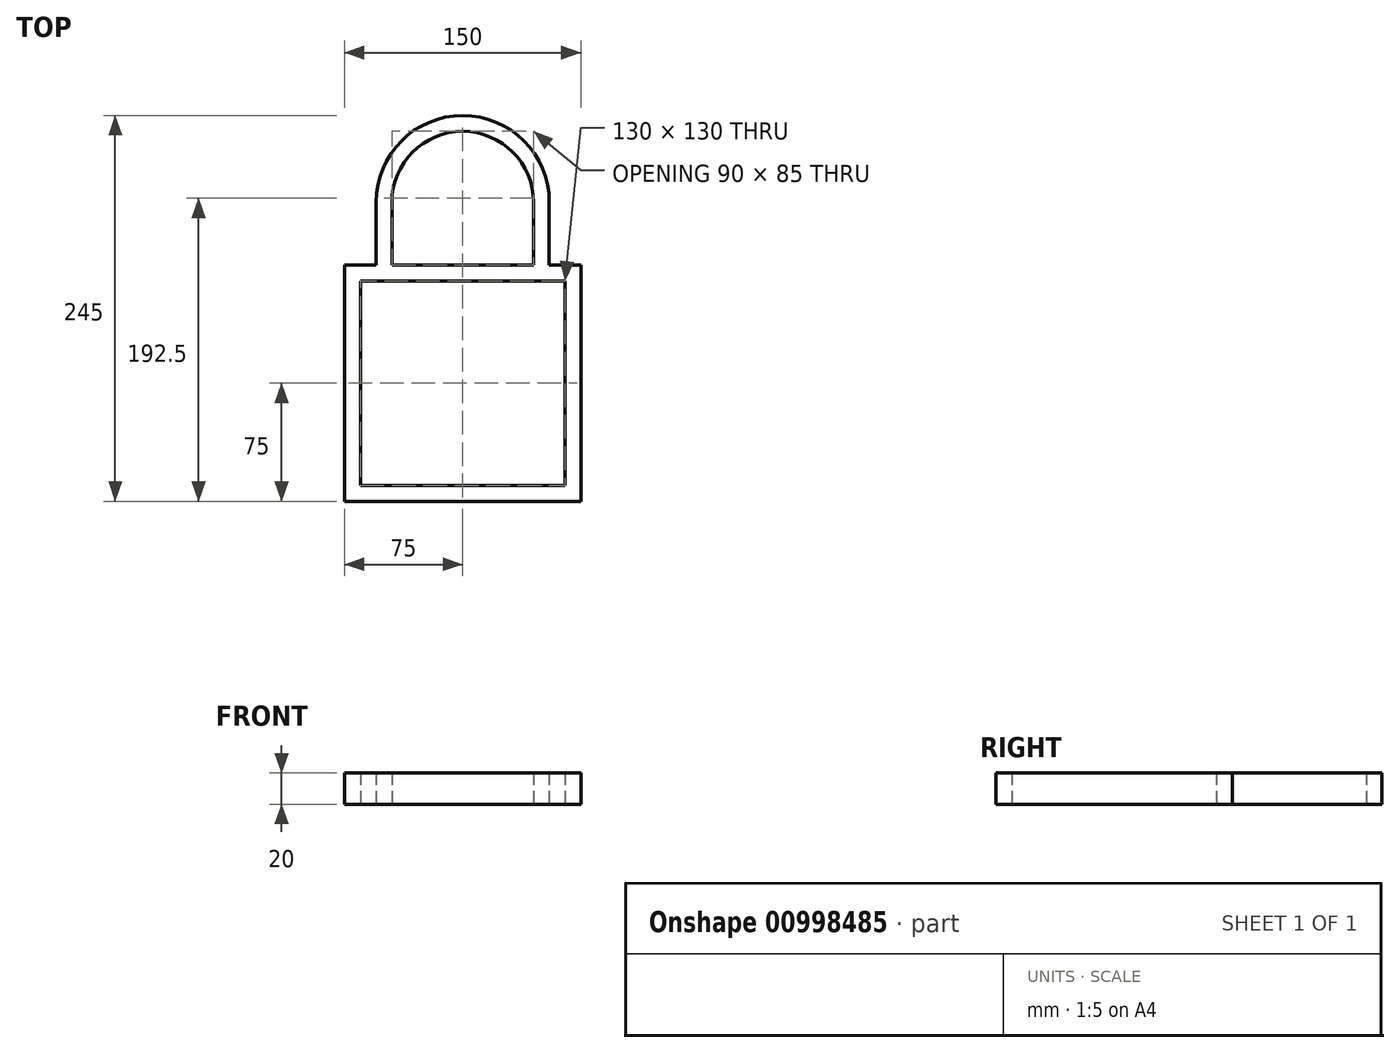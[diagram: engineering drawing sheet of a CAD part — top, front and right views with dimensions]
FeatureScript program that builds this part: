
annotation { "Feature Type Name" : "Feature", "Feature Type Description" : "" }
export const myFeature = defineFeature(function(context is Context, id is Id, definition is map)
    precondition{}
    {
        {
            var Q0;
            Q0=qCreatedBy(makeId("Top.planeOp"),FACE);
            var sketch = newSketch(context, id + "F0", { "sketchPlane" : qUnion([Q0])});
            skLineSegment(sketch, "E0.bottom", {"start": v(75, 75) * mm, "end": v(-75, 75) * mm});
            skLineSegment(sketch, "E0.top", {"start": v(75, -75) * mm, "end": v(-75, -75) * mm});
            skLineSegment(sketch, "E0.left", {"start": v(75, 75) * mm, "end": v(75, -75) * mm});
            skLineSegment(sketch, "E0.right", {"start": v(-75, 75) * mm, "end": v(-75, -75) * mm});
            skPoint(sketch, "E0.middle", {"position": v(0, 0) * mm});
            skLineSegment(sketch, "E1.bottom", {"start": v(65, 65) * mm, "end": v(-65, 65) * mm});
            skLineSegment(sketch, "E1.top", {"start": v(65, -65) * mm, "end": v(-65, -65) * mm});
            skLineSegment(sketch, "E1.left", {"start": v(65, 65) * mm, "end": v(65, -65) * mm});
            skLineSegment(sketch, "E1.right", {"start": v(-65, 65) * mm, "end": v(-65, -65) * mm});
            skLineSegment(sketch, "E2.bottom", {"start": v(55, 115) * mm, "end": v(-55, 115) * mm});
            skLineSegment(sketch, "E2.top", {"start": v(55, 35) * mm, "end": v(-55, 35) * mm});
            skLineSegment(sketch, "E2.left", {"start": v(55, 115) * mm, "end": v(55, 35) * mm});
            skLineSegment(sketch, "E2.right", {"start": v(-55, 115) * mm, "end": v(-55, 35) * mm});
            skPoint(sketch, "E2.middle", {"position": v(0, 75) * mm});
            skLineSegment(sketch, "E3.bottom", {"start": v(45, 115) * mm, "end": v(-45, 115) * mm});
            skLineSegment(sketch, "E3.top", {"start": v(45, 35) * mm, "end": v(-45, 35) * mm});
            skLineSegment(sketch, "E3.left", {"start": v(45, 115) * mm, "end": v(45, 35) * mm});
            skLineSegment(sketch, "E3.right", {"start": v(-45, 115) * mm, "end": v(-45, 35) * mm});
            skCircle(sketch, "E4", {"center": v(0, 115) * mm, "radius": 55 * mm});
            skCircle(sketch, "E5", {"center": v(0, 115) * mm, "radius": 45 * mm});
            skSolve(sketch);
        }
        {
            var Q0;
            Q0=makeQuery(id+"F0.imprint","IMPRINT",FACE,{"disambiguationData":[TD([[makeQuery(id+"F0.imprint","IMPRINT",EDGE,{"derivedFrom":sQuery(id+"F0.wireOp",EDGE,"E0.top")}),-1.0]])]});
            var Q1;
            {var subQ0=sQuery(id+"F0.wireOp",EDGE,"E2.right");var subQ1=sQuery(id+"F0.wireOp",EDGE,"E0.bottom");var subQ2=makeQuery(id+"F0.imprint","INTERSECT",VERTEX,{"derivedFrom":[subQ1,subQ0]});Q1=makeQuery(id+"F0.imprint","IMPRINT",FACE,{"disambiguationData":[TD([[makeQuery(id+"F0.imprint","IMPRINT",EDGE,{"disambiguationData":[TD([[subQ2,1.0]])],"derivedFrom":subQ1}),1.0]])]});}
            var Q2;
            {var subQ0=sQuery(id+"F0.wireOp",EDGE,"E5");var subQ1=sQuery(id+"F0.wireOp",EDGE,"E0.bottom");var subQ2=makeQuery(id+"F0.imprint","INTERSECT",VERTEX,{"disambiguationData":[OD(0.0)],"derivedFrom":[subQ1,subQ0]});Q2=makeQuery(id+"F0.imprint","IMPRINT",FACE,{"disambiguationData":[TD([[makeQuery(id+"F0.imprint","IMPRINT",EDGE,{"disambiguationData":[TD([[subQ2,-1.0]])],"derivedFrom":subQ1}),1.0]])]});}
            var Q3;
            {var subQ0=sQuery(id+"F0.wireOp",EDGE,"E5");var subQ1=sQuery(id+"F0.wireOp",EDGE,"E0.bottom");var subQ2=makeQuery(id+"F0.imprint","INTERSECT",VERTEX,{"disambiguationData":[OD(1.0)],"derivedFrom":[subQ1,subQ0]});Q3=makeQuery(id+"F0.imprint","IMPRINT",FACE,{"disambiguationData":[TD([[makeQuery(id+"F0.imprint","IMPRINT",EDGE,{"disambiguationData":[TD([[subQ2,-1.0]])],"derivedFrom":subQ1}),1.0]])]});}
            var Q4;
            {var subQ0=sQuery(id+"F0.wireOp",EDGE,"E4");var subQ1=sQuery(id+"F0.wireOp",EDGE,"E0.bottom");var subQ2=makeQuery(id+"F0.imprint","INTERSECT",VERTEX,{"disambiguationData":[OD(1.0)],"derivedFrom":[subQ1,subQ0]});Q4=makeQuery(id+"F0.imprint","IMPRINT",FACE,{"disambiguationData":[TD([[makeQuery(id+"F0.imprint","IMPRINT",EDGE,{"disambiguationData":[TD([[subQ2,-1.0]])],"derivedFrom":subQ1}),1.0]])]});}
            var Q5;
            {var subQ0=sQuery(id+"F0.wireOp",EDGE,"E4");var subQ1=sQuery(id+"F0.wireOp",EDGE,"E0.bottom");var subQ2=makeQuery(id+"F0.imprint","INTERSECT",VERTEX,{"disambiguationData":[OD(0.0)],"derivedFrom":[subQ1,subQ0]});Q5=makeQuery(id+"F0.imprint","IMPRINT",FACE,{"disambiguationData":[TD([[makeQuery(id+"F0.imprint","IMPRINT",EDGE,{"disambiguationData":[TD([[subQ2,-1.0]])],"derivedFrom":subQ1}),1.0]])]});}
            var Q6;
            {var subQ0=sQuery(id+"F0.wireOp",EDGE,"E3.left");var subQ1=sQuery(id+"F0.wireOp",EDGE,"E0.bottom");var subQ2=makeQuery(id+"F0.imprint","INTERSECT",VERTEX,{"derivedFrom":[subQ1,subQ0]});Q6=makeQuery(id+"F0.imprint","IMPRINT",FACE,{"disambiguationData":[TD([[makeQuery(id+"F0.imprint","IMPRINT",EDGE,{"disambiguationData":[TD([[subQ2,-1.0]])],"derivedFrom":subQ1}),1.0]])]});}
            var Q7;
            {var subQ0=sQuery(id+"F0.wireOp",EDGE,"E2.left");var subQ1=sQuery(id+"F0.wireOp",EDGE,"E0.bottom");var subQ2=makeQuery(id+"F0.imprint","INTERSECT",VERTEX,{"derivedFrom":[subQ1,subQ0]});Q7=makeQuery(id+"F0.imprint","IMPRINT",FACE,{"disambiguationData":[TD([[makeQuery(id+"F0.imprint","IMPRINT",EDGE,{"disambiguationData":[TD([[subQ2,-1.0]])],"derivedFrom":subQ1}),1.0]])]});}
            var Q8;
            {var subQ0=sQuery(id+"F0.wireOp",EDGE,"E2.left");var subQ1=sQuery(id+"F0.wireOp",EDGE,"E0.bottom");var subQ2=makeQuery(id+"F0.imprint","INTERSECT",VERTEX,{"derivedFrom":[subQ1,subQ0]});Q8=makeQuery(id+"F0.imprint","IMPRINT",FACE,{"disambiguationData":[TD([[makeQuery(id+"F0.imprint","IMPRINT",EDGE,{"disambiguationData":[TD([[subQ2,-1.0]])],"derivedFrom":subQ1}),-1.0]])]});}
            var Q9;
            {var subQ0=sQuery(id+"F0.wireOp",EDGE,"E4");var subQ3=sQuery(id+"F0.wireOp",EDGE,"E3.left");var subQ5=makeQuery(id+"F0.imprint","INTERSECT",VERTEX,{"derivedFrom":[subQ3,subQ0]});Q9=makeQuery(id+"F0.imprint","IMPRINT",FACE,{"disambiguationData":[TD([[makeQuery(id+"F0.imprint","IMPRINT",EDGE,{"disambiguationData":[TD([[subQ5,-1.0]])],"derivedFrom":subQ0}),1.0]])]});}
            var Q10;
            {var subQ0=sQuery(id+"F0.wireOp",EDGE,"E2.right");var subQ1=sQuery(id+"F0.wireOp",EDGE,"E0.bottom");var subQ2=makeQuery(id+"F0.imprint","INTERSECT",VERTEX,{"derivedFrom":[subQ1,subQ0]});Q10=makeQuery(id+"F0.imprint","IMPRINT",FACE,{"disambiguationData":[TD([[makeQuery(id+"F0.imprint","IMPRINT",EDGE,{"disambiguationData":[TD([[subQ2,1.0]])],"derivedFrom":subQ1}),-1.0]])]});}
            var Q11;
            {var subQ0=sQuery(id+"F0.wireOp",EDGE,"E4");var subQ3=sQuery(id+"F0.wireOp",EDGE,"E3.right");var subQ5=makeQuery(id+"F0.imprint","INTERSECT",VERTEX,{"derivedFrom":[subQ3,subQ0]});Q11=makeQuery(id+"F0.imprint","IMPRINT",FACE,{"disambiguationData":[TD([[makeQuery(id+"F0.imprint","IMPRINT",EDGE,{"disambiguationData":[TD([[subQ5,1.0]])],"derivedFrom":subQ0}),1.0]])]});}
            var Q12;
            {var subQ0=sQuery(id+"F0.wireOp",EDGE,"E4");var subQ1=sQuery(id+"F0.wireOp",EDGE,"E2.bottom");var subQ2=makeQuery(id+"F0.imprint","INTERSECT",VERTEX,{"derivedFrom":[subQ1,sQuery(id+"F0.wireOp",EDGE,"E2.left"),subQ0]});Q12=makeQuery(id+"F0.imprint","IMPRINT",FACE,{"disambiguationData":[TD([[makeQuery(id+"F0.imprint","IMPRINT",EDGE,{"disambiguationData":[TD([[subQ2,-1.0]])],"derivedFrom":subQ0}),1.0]])]});}
            extrude(context, id + "F1", {"entities" : qUnion([Q0, Q1, Q2, Q3, Q4, Q5, Q6, Q7, Q8, Q9, Q10, Q11, Q12]), "depth" : 20 * mm, "offsetDistance" : 25 * mm});
        }
    });
